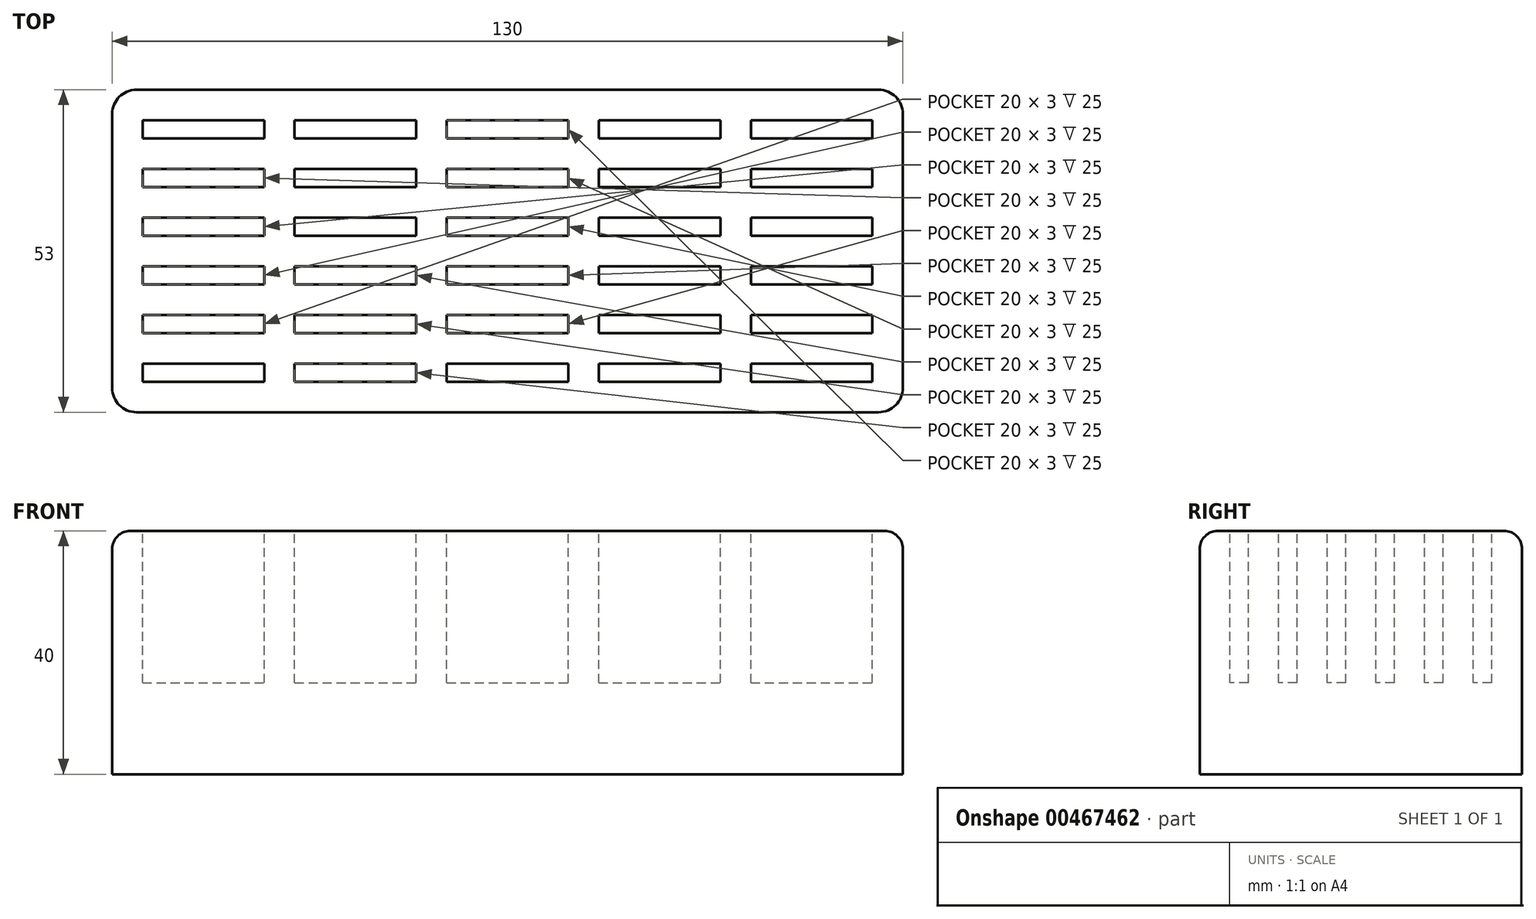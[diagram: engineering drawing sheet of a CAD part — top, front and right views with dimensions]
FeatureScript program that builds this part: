
annotation { "Feature Type Name" : "Feature", "Feature Type Description" : "" }
export const myFeature = defineFeature(function(context is Context, id is Id, definition is map)
    precondition{}
    {
        {
            var Q0;
            Q0=qCreatedBy(makeId("Top.planeOp"),FACE);
            var sketch = newSketch(context, id + "F0", { "sketchPlane" : qUnion([Q0])});
            skLineSegment(sketch, "E0.bottom", {"start": v(4, 0) * mm, "end": v(126, 0) * mm});
            skLineSegment(sketch, "E0.top", {"start": v(4, 53) * mm, "end": v(126, 53) * mm});
            skLineSegment(sketch, "E0.left", {"start": v(0, 4) * mm, "end": v(0, 49) * mm});
            skLineSegment(sketch, "E0.right", {"start": v(130, 4) * mm, "end": v(130, 49) * mm});
            skPoint(sketch, "E1.visualSharp", {"position": v(0, 53) * mm});
            skArc(sketch, "E1.filletArc", {"start": v(4, 53) * mm, "mid": v(1.17, 51.83) * mm, "end": v(0, 49) * mm});
            skPoint(sketch, "E2.visualSharp", {"position": v(130, 53) * mm});
            skArc(sketch, "E2.filletArc", {"start": v(130, 49) * mm, "mid": v(128.83, 51.83) * mm, "end": v(126, 53) * mm});
            skPoint(sketch, "E3.visualSharp", {"position": v(130, 0) * mm});
            skArc(sketch, "E3.filletArc", {"start": v(126, 0) * mm, "mid": v(128.83, 1.17) * mm, "end": v(130, 4) * mm});
            skPoint(sketch, "E4.visualSharp", {"position": v(0, 0) * mm});
            skArc(sketch, "E4.filletArc", {"start": v(0, 4) * mm, "mid": v(1.17, 1.17) * mm, "end": v(4, 0) * mm});
            skSolve(sketch);
        }
        {
            var Q0;
            Q0 = qSketchRegion(id + "F0", true);
            extrude(context, id + "F1", {"entities" : qUnion([Q0]), "depth" : 40 * mm});
        }
        {
            var Q0;
            Q0=makeQuery(id+"F1.opExtrude","CAP_FACE",FACE,{"disambiguationData":[OSD([sQuery(id+"F0.wireOp",EDGE,"E0.bottom"),sQuery(id+"F0.wireOp",EDGE,"E0.top"),sQuery(id+"F0.wireOp",EDGE,"E0.left"),sQuery(id+"F0.wireOp",EDGE,"E0.right"),sQuery(id+"F0.wireOp",EDGE,"E1.filletArc"),sQuery(id+"F0.wireOp",EDGE,"E2.filletArc"),sQuery(id+"F0.wireOp",EDGE,"E3.filletArc"),sQuery(id+"F0.wireOp",EDGE,"E4.filletArc")])],"isStart":false});
            var sketch = newSketch(context, id + "F2", { "sketchPlane" : qUnion([Q0])});
            skLineSegment(sketch, "E5.bottom", {"start": v(5, 48) * mm, "end": v(25, 48) * mm});
            skLineSegment(sketch, "E5.top", {"start": v(5, 45) * mm, "end": v(25, 45) * mm});
            skLineSegment(sketch, "E5.left", {"start": v(5, 48) * mm, "end": v(5, 45) * mm});
            skLineSegment(sketch, "E5.right", {"start": v(25, 48) * mm, "end": v(25, 45) * mm});
            skLineSegment(sketch, "E6.0.1.0", {"start": v(25, 40) * mm, "end": v(25, 37) * mm});
            skLineSegment(sketch, "E6.0.1.1", {"start": v(5, 40) * mm, "end": v(5, 37) * mm});
            skLineSegment(sketch, "E6.0.1.2", {"start": v(5, 37) * mm, "end": v(25, 37) * mm});
            skLineSegment(sketch, "E6.0.1.3", {"start": v(5, 40) * mm, "end": v(25, 40) * mm});
            skLineSegment(sketch, "E6.0.2.0", {"start": v(25, 32) * mm, "end": v(25, 29) * mm});
            skLineSegment(sketch, "E6.0.2.1", {"start": v(5, 32) * mm, "end": v(5, 29) * mm});
            skLineSegment(sketch, "E6.0.2.2", {"start": v(5, 29) * mm, "end": v(25, 29) * mm});
            skLineSegment(sketch, "E6.0.2.3", {"start": v(5, 32) * mm, "end": v(25, 32) * mm});
            skLineSegment(sketch, "E6.0.3.0", {"start": v(25, 24) * mm, "end": v(25, 21) * mm});
            skLineSegment(sketch, "E6.0.3.1", {"start": v(5, 24) * mm, "end": v(5, 21) * mm});
            skLineSegment(sketch, "E6.0.3.2", {"start": v(5, 21) * mm, "end": v(25, 21) * mm});
            skLineSegment(sketch, "E6.0.3.3", {"start": v(5, 24) * mm, "end": v(25, 24) * mm});
            skLineSegment(sketch, "E6.0.4.0", {"start": v(25, 16) * mm, "end": v(25, 13) * mm});
            skLineSegment(sketch, "E6.0.4.1", {"start": v(5, 16) * mm, "end": v(5, 13) * mm});
            skLineSegment(sketch, "E6.0.4.2", {"start": v(5, 13) * mm, "end": v(25, 13) * mm});
            skLineSegment(sketch, "E6.0.4.3", {"start": v(5, 16) * mm, "end": v(25, 16) * mm});
            skLineSegment(sketch, "E6.0.5.0", {"start": v(25, 8) * mm, "end": v(25, 5) * mm});
            skLineSegment(sketch, "E6.0.5.1", {"start": v(5, 8) * mm, "end": v(5, 5) * mm});
            skLineSegment(sketch, "E6.0.5.2", {"start": v(5, 5) * mm, "end": v(25, 5) * mm});
            skLineSegment(sketch, "E6.0.5.3", {"start": v(5, 8) * mm, "end": v(25, 8) * mm});
            skLineSegment(sketch, "E6.1.0.0", {"start": v(50, 48) * mm, "end": v(50, 45) * mm});
            skLineSegment(sketch, "E6.1.0.1", {"start": v(30, 48) * mm, "end": v(30, 45) * mm});
            skLineSegment(sketch, "E6.1.0.2", {"start": v(30, 45) * mm, "end": v(50, 45) * mm});
            skLineSegment(sketch, "E6.1.0.3", {"start": v(30, 48) * mm, "end": v(50, 48) * mm});
            skLineSegment(sketch, "E6.1.1.0", {"start": v(50, 40) * mm, "end": v(50, 37) * mm});
            skLineSegment(sketch, "E6.1.1.1", {"start": v(30, 40) * mm, "end": v(30, 37) * mm});
            skLineSegment(sketch, "E6.1.1.2", {"start": v(30, 37) * mm, "end": v(50, 37) * mm});
            skLineSegment(sketch, "E6.1.1.3", {"start": v(30, 40) * mm, "end": v(50, 40) * mm});
            skLineSegment(sketch, "E6.1.2.0", {"start": v(50, 32) * mm, "end": v(50, 29) * mm});
            skLineSegment(sketch, "E6.1.2.1", {"start": v(30, 32) * mm, "end": v(30, 29) * mm});
            skLineSegment(sketch, "E6.1.2.2", {"start": v(30, 29) * mm, "end": v(50, 29) * mm});
            skLineSegment(sketch, "E6.1.2.3", {"start": v(30, 32) * mm, "end": v(50, 32) * mm});
            skLineSegment(sketch, "E6.1.3.0", {"start": v(50, 24) * mm, "end": v(50, 21) * mm});
            skLineSegment(sketch, "E6.1.3.1", {"start": v(30, 24) * mm, "end": v(30, 21) * mm});
            skLineSegment(sketch, "E6.1.3.2", {"start": v(30, 21) * mm, "end": v(50, 21) * mm});
            skLineSegment(sketch, "E6.1.3.3", {"start": v(30, 24) * mm, "end": v(50, 24) * mm});
            skLineSegment(sketch, "E6.1.4.0", {"start": v(50, 16) * mm, "end": v(50, 13) * mm});
            skLineSegment(sketch, "E6.1.4.1", {"start": v(30, 16) * mm, "end": v(30, 13) * mm});
            skLineSegment(sketch, "E6.1.4.2", {"start": v(30, 13) * mm, "end": v(50, 13) * mm});
            skLineSegment(sketch, "E6.1.4.3", {"start": v(30, 16) * mm, "end": v(50, 16) * mm});
            skLineSegment(sketch, "E6.1.5.0", {"start": v(50, 8) * mm, "end": v(50, 5) * mm});
            skLineSegment(sketch, "E6.1.5.1", {"start": v(30, 8) * mm, "end": v(30, 5) * mm});
            skLineSegment(sketch, "E6.1.5.2", {"start": v(30, 5) * mm, "end": v(50, 5) * mm});
            skLineSegment(sketch, "E6.1.5.3", {"start": v(30, 8) * mm, "end": v(50, 8) * mm});
            skLineSegment(sketch, "E6.2.0.0", {"start": v(75, 48) * mm, "end": v(75, 45) * mm});
            skLineSegment(sketch, "E6.2.0.1", {"start": v(55, 48) * mm, "end": v(55, 45) * mm});
            skLineSegment(sketch, "E6.2.0.2", {"start": v(55, 45) * mm, "end": v(75, 45) * mm});
            skLineSegment(sketch, "E6.2.0.3", {"start": v(55, 48) * mm, "end": v(75, 48) * mm});
            skLineSegment(sketch, "E6.2.1.0", {"start": v(75, 40) * mm, "end": v(75, 37) * mm});
            skLineSegment(sketch, "E6.2.1.1", {"start": v(55, 40) * mm, "end": v(55, 37) * mm});
            skLineSegment(sketch, "E6.2.1.2", {"start": v(55, 37) * mm, "end": v(75, 37) * mm});
            skLineSegment(sketch, "E6.2.1.3", {"start": v(55, 40) * mm, "end": v(75, 40) * mm});
            skLineSegment(sketch, "E6.2.2.0", {"start": v(75, 32) * mm, "end": v(75, 29) * mm});
            skLineSegment(sketch, "E6.2.2.1", {"start": v(55, 32) * mm, "end": v(55, 29) * mm});
            skLineSegment(sketch, "E6.2.2.2", {"start": v(55, 29) * mm, "end": v(75, 29) * mm});
            skLineSegment(sketch, "E6.2.2.3", {"start": v(55, 32) * mm, "end": v(75, 32) * mm});
            skLineSegment(sketch, "E6.2.3.0", {"start": v(75, 24) * mm, "end": v(75, 21) * mm});
            skLineSegment(sketch, "E6.2.3.1", {"start": v(55, 24) * mm, "end": v(55, 21) * mm});
            skLineSegment(sketch, "E6.2.3.2", {"start": v(55, 21) * mm, "end": v(75, 21) * mm});
            skLineSegment(sketch, "E6.2.3.3", {"start": v(55, 24) * mm, "end": v(75, 24) * mm});
            skLineSegment(sketch, "E6.2.4.0", {"start": v(75, 16) * mm, "end": v(75, 13) * mm});
            skLineSegment(sketch, "E6.2.4.1", {"start": v(55, 16) * mm, "end": v(55, 13) * mm});
            skLineSegment(sketch, "E6.2.4.2", {"start": v(55, 13) * mm, "end": v(75, 13) * mm});
            skLineSegment(sketch, "E6.2.4.3", {"start": v(55, 16) * mm, "end": v(75, 16) * mm});
            skLineSegment(sketch, "E6.2.5.0", {"start": v(75, 8) * mm, "end": v(75, 5) * mm});
            skLineSegment(sketch, "E6.2.5.1", {"start": v(55, 8) * mm, "end": v(55, 5) * mm});
            skLineSegment(sketch, "E6.2.5.2", {"start": v(55, 5) * mm, "end": v(75, 5) * mm});
            skLineSegment(sketch, "E6.2.5.3", {"start": v(55, 8) * mm, "end": v(75, 8) * mm});
            skLineSegment(sketch, "E6.3.0.0", {"start": v(100, 48) * mm, "end": v(100, 45) * mm});
            skLineSegment(sketch, "E6.3.0.1", {"start": v(80, 48) * mm, "end": v(80, 45) * mm});
            skLineSegment(sketch, "E6.3.0.2", {"start": v(80, 45) * mm, "end": v(100, 45) * mm});
            skLineSegment(sketch, "E6.3.0.3", {"start": v(80, 48) * mm, "end": v(100, 48) * mm});
            skLineSegment(sketch, "E6.3.1.0", {"start": v(100, 40) * mm, "end": v(100, 37) * mm});
            skLineSegment(sketch, "E6.3.1.1", {"start": v(80, 40) * mm, "end": v(80, 37) * mm});
            skLineSegment(sketch, "E6.3.1.2", {"start": v(80, 37) * mm, "end": v(100, 37) * mm});
            skLineSegment(sketch, "E6.3.1.3", {"start": v(80, 40) * mm, "end": v(100, 40) * mm});
            skLineSegment(sketch, "E6.3.2.0", {"start": v(100, 32) * mm, "end": v(100, 29) * mm});
            skLineSegment(sketch, "E6.3.2.1", {"start": v(80, 32) * mm, "end": v(80, 29) * mm});
            skLineSegment(sketch, "E6.3.2.2", {"start": v(80, 29) * mm, "end": v(100, 29) * mm});
            skLineSegment(sketch, "E6.3.2.3", {"start": v(80, 32) * mm, "end": v(100, 32) * mm});
            skLineSegment(sketch, "E6.3.3.0", {"start": v(100, 24) * mm, "end": v(100, 21) * mm});
            skLineSegment(sketch, "E6.3.3.1", {"start": v(80, 24) * mm, "end": v(80, 21) * mm});
            skLineSegment(sketch, "E6.3.3.2", {"start": v(80, 21) * mm, "end": v(100, 21) * mm});
            skLineSegment(sketch, "E6.3.3.3", {"start": v(80, 24) * mm, "end": v(100, 24) * mm});
            skLineSegment(sketch, "E6.3.4.0", {"start": v(100, 16) * mm, "end": v(100, 13) * mm});
            skLineSegment(sketch, "E6.3.4.1", {"start": v(80, 16) * mm, "end": v(80, 13) * mm});
            skLineSegment(sketch, "E6.3.4.2", {"start": v(80, 13) * mm, "end": v(100, 13) * mm});
            skLineSegment(sketch, "E6.3.4.3", {"start": v(80, 16) * mm, "end": v(100, 16) * mm});
            skLineSegment(sketch, "E6.3.5.0", {"start": v(100, 8) * mm, "end": v(100, 5) * mm});
            skLineSegment(sketch, "E6.3.5.1", {"start": v(80, 8) * mm, "end": v(80, 5) * mm});
            skLineSegment(sketch, "E6.3.5.2", {"start": v(80, 5) * mm, "end": v(100, 5) * mm});
            skLineSegment(sketch, "E6.3.5.3", {"start": v(80, 8) * mm, "end": v(100, 8) * mm});
            skLineSegment(sketch, "E6.4.0.0", {"start": v(125, 48) * mm, "end": v(125, 45) * mm});
            skLineSegment(sketch, "E6.4.0.1", {"start": v(105, 48) * mm, "end": v(105, 45) * mm});
            skLineSegment(sketch, "E6.4.0.2", {"start": v(105, 45) * mm, "end": v(125, 45) * mm});
            skLineSegment(sketch, "E6.4.0.3", {"start": v(105, 48) * mm, "end": v(125, 48) * mm});
            skLineSegment(sketch, "E6.4.1.0", {"start": v(125, 40) * mm, "end": v(125, 37) * mm});
            skLineSegment(sketch, "E6.4.1.1", {"start": v(105, 40) * mm, "end": v(105, 37) * mm});
            skLineSegment(sketch, "E6.4.1.2", {"start": v(105, 37) * mm, "end": v(125, 37) * mm});
            skLineSegment(sketch, "E6.4.1.3", {"start": v(105, 40) * mm, "end": v(125, 40) * mm});
            skLineSegment(sketch, "E6.4.2.0", {"start": v(125, 32) * mm, "end": v(125, 29) * mm});
            skLineSegment(sketch, "E6.4.2.1", {"start": v(105, 32) * mm, "end": v(105, 29) * mm});
            skLineSegment(sketch, "E6.4.2.2", {"start": v(105, 29) * mm, "end": v(125, 29) * mm});
            skLineSegment(sketch, "E6.4.2.3", {"start": v(105, 32) * mm, "end": v(125, 32) * mm});
            skLineSegment(sketch, "E6.4.3.0", {"start": v(125, 24) * mm, "end": v(125, 21) * mm});
            skLineSegment(sketch, "E6.4.3.1", {"start": v(105, 24) * mm, "end": v(105, 21) * mm});
            skLineSegment(sketch, "E6.4.3.2", {"start": v(105, 21) * mm, "end": v(125, 21) * mm});
            skLineSegment(sketch, "E6.4.3.3", {"start": v(105, 24) * mm, "end": v(125, 24) * mm});
            skLineSegment(sketch, "E6.4.4.0", {"start": v(125, 16) * mm, "end": v(125, 13) * mm});
            skLineSegment(sketch, "E6.4.4.1", {"start": v(105, 16) * mm, "end": v(105, 13) * mm});
            skLineSegment(sketch, "E6.4.4.2", {"start": v(105, 13) * mm, "end": v(125, 13) * mm});
            skLineSegment(sketch, "E6.4.4.3", {"start": v(105, 16) * mm, "end": v(125, 16) * mm});
            skLineSegment(sketch, "E6.4.5.0", {"start": v(125, 8) * mm, "end": v(125, 5) * mm});
            skLineSegment(sketch, "E6.4.5.1", {"start": v(105, 8) * mm, "end": v(105, 5) * mm});
            skLineSegment(sketch, "E6.4.5.2", {"start": v(105, 5) * mm, "end": v(125, 5) * mm});
            skLineSegment(sketch, "E6.4.5.3", {"start": v(105, 8) * mm, "end": v(125, 8) * mm});
            skLineSegment(sketch, "E6.direction1", {"start": v(5, 45) * mm, "end": v(30, 45) * mm, "construction": true});
            skLineSegment(sketch, "E6.direction2", {"start": v(5, 45) * mm, "end": v(5, 37) * mm, "construction": true});
            skSolve(sketch);
        }
        {
            var Q0;
            Q0 = qSketchRegion(id + "F2", true);
            extrude(context, id + "F3", {"entities" : qUnion([Q0]), "operationType" : NewBodyOperationType.REMOVE, "oppositeDirection" : true, "depth" : 25 * mm});
        }
        {
            var Q0;
            Q0=makeQuery(id+"F1.opExtrude","CAP_EDGE",EDGE,{"disambiguationData":[OSD([sQuery(id+"F0.wireOp",EDGE,"E0.top")])],"isStart":false});
            var Q1;
            Q1=makeQuery(id+"F1.opExtrude","CAP_EDGE",EDGE,{"disambiguationData":[OSD([sQuery(id+"F0.wireOp",EDGE,"E1.filletArc")])],"isStart":false});
            fillet(context, id + "F4", {"entities" : qUnion([Q0, Q1]), "radius" : 3 * mm, "tangentPropagation" : true, "allowEdgeOverflow" : false});
        }
    });
